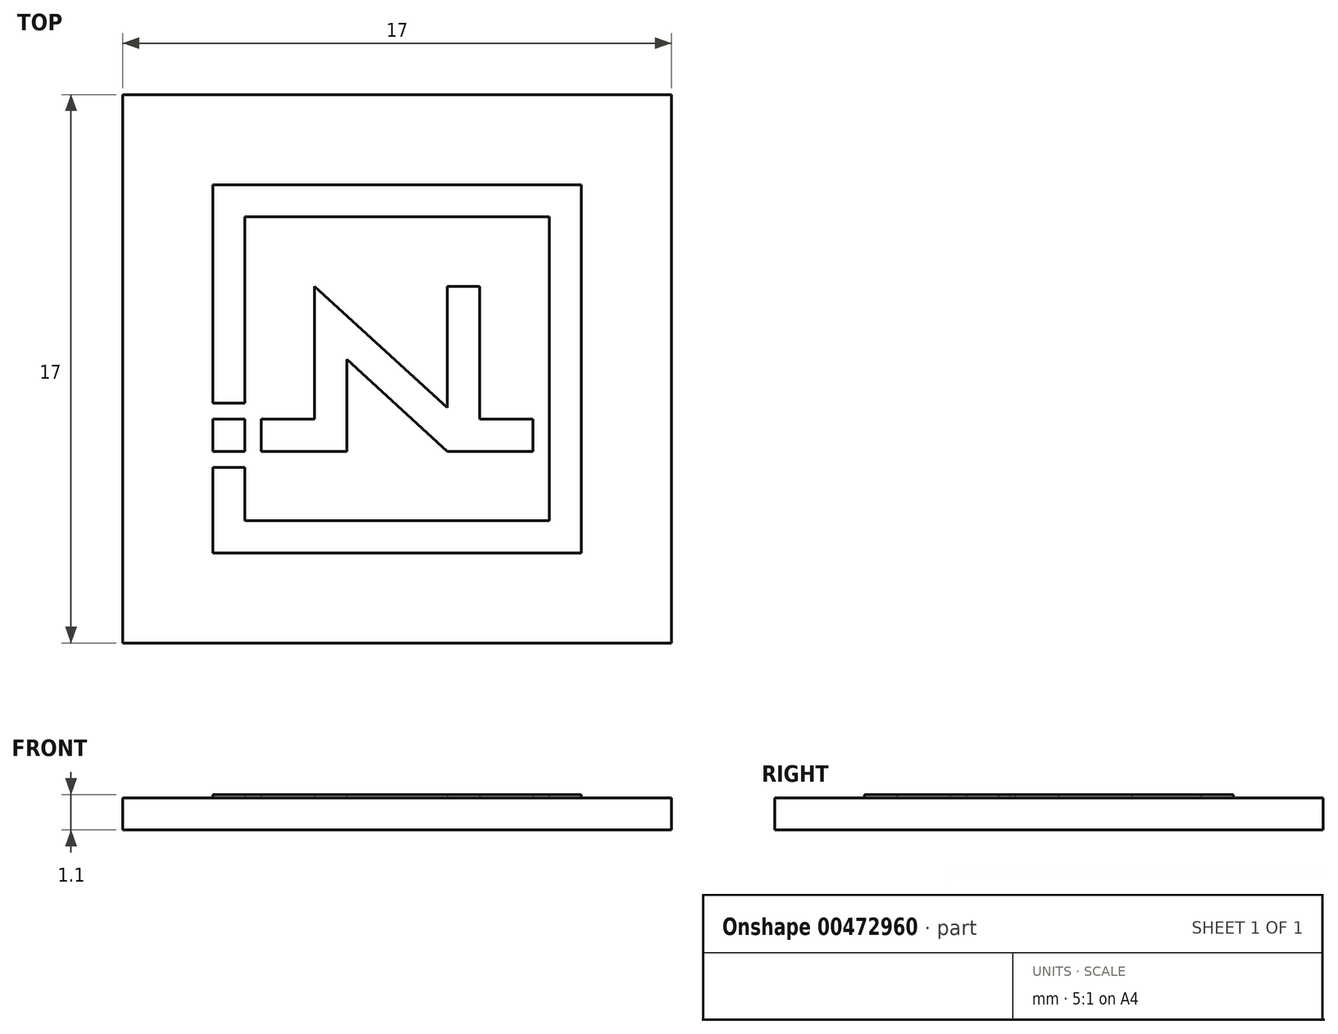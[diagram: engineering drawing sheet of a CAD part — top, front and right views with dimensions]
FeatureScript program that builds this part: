
annotation { "Feature Type Name" : "Feature", "Feature Type Description" : "" }
export const myFeature = defineFeature(function(context is Context, id is Id, definition is map)
    precondition{}
    {
        {
            var Q0;
            Q0=qCreatedBy(makeId("Top.planeOp"),FACE);
            var sketch = newSketch(context, id + "F0", { "sketchPlane" : qUnion([Q0])});
            skLineSegment(sketch, "E0.bottom", {"start": v(-5.71, 5.71) * mm, "end": v(5.71, 5.71) * mm});
            skLineSegment(sketch, "E0.top", {"start": v(-5.71, -5.71) * mm, "end": v(5.71, -5.71) * mm});
            skLineSegment(sketch, "E0.left", {"start": v(-5.71, 5.71) * mm, "end": v(-5.71, -5.71) * mm, "construction": true});
            skLineSegment(sketch, "E0.right", {"start": v(5.71, 5.71) * mm, "end": v(5.71, -5.71) * mm});
            skPoint(sketch, "E0.middle", {"position": v(0, 0) * mm});
            skLineSegment(sketch, "E1.0", {"start": v(4.71, 4.71) * mm, "end": v(4.71, -4.71) * mm});
            skLineSegment(sketch, "E1.1", {"start": v(-4.71, 4.71) * mm, "end": v(4.71, 4.71) * mm});
            skLineSegment(sketch, "E1.2", {"start": v(-4.71, 4.71) * mm, "end": v(-4.71, -4.71) * mm, "construction": true});
            skLineSegment(sketch, "E1.3", {"start": v(-4.71, -4.71) * mm, "end": v(4.71, -4.71) * mm});
            skLineSegment(sketch, "E2.bottom", {"start": v(8, 2.56) * mm, "end": v(-8, 2.56) * mm, "construction": true});
            skLineSegment(sketch, "E2.top", {"start": v(8, -2.56) * mm, "end": v(-8, -2.56) * mm, "construction": true});
            skLineSegment(sketch, "E2.left", {"start": v(8, 2.56) * mm, "end": v(8, -2.56) * mm, "construction": true});
            skLineSegment(sketch, "E2.right", {"start": v(-8, 2.56) * mm, "end": v(-8, -2.56) * mm, "construction": true});
            skLineSegment(sketch, "E3.bottom", {"start": v(-5.71, -2.56) * mm, "end": v(-4.71, -2.56) * mm});
            skLineSegment(sketch, "E3.top", {"start": v(-5.71, -1.56) * mm, "end": v(-4.71, -1.56) * mm});
            skLineSegment(sketch, "E3.left", {"start": v(-5.71, -2.56) * mm, "end": v(-5.71, -1.56) * mm});
            skLineSegment(sketch, "E3.right", {"start": v(-4.71, -2.56) * mm, "end": v(-4.71, -1.56) * mm});
            skLineSegment(sketch, "E4", {"start": v(-5.71, -5.71) * mm, "end": v(-5.71, -3.06) * mm});
            skLineSegment(sketch, "E5", {"start": v(-5.71, -3.06) * mm, "end": v(-4.71, -3.06) * mm});
            skLineSegment(sketch, "E6", {"start": v(-4.71, -3.06) * mm, "end": v(-4.71, -4.71) * mm});
            skLineSegment(sketch, "E7", {"start": v(-5.71, 5.71) * mm, "end": v(-5.71, -1.06) * mm});
            skLineSegment(sketch, "E8", {"start": v(-5.71, -1.06) * mm, "end": v(-4.71, -1.06) * mm});
            skLineSegment(sketch, "E9", {"start": v(-4.71, -1.06) * mm, "end": v(-4.71, 4.71) * mm});
            skLineSegment(sketch, "E10.bottom", {"start": v(-2.56, 2.56) * mm, "end": v(2.56, 2.56) * mm, "construction": true});
            skLineSegment(sketch, "E10.top", {"start": v(-2.56, -2.56) * mm, "end": v(2.56, -2.56) * mm, "construction": true});
            skLineSegment(sketch, "E10.left", {"start": v(-2.56, 2.56) * mm, "end": v(-2.56, -2.56) * mm, "construction": true});
            skLineSegment(sketch, "E10.right", {"start": v(2.56, 2.56) * mm, "end": v(2.56, -2.56) * mm, "construction": true});
            skLineSegment(sketch, "E11", {"start": v(-4.21, -2.56) * mm, "end": v(-4.21, -1.56) * mm});
            skLineSegment(sketch, "E12", {"start": v(-4.21, -1.56) * mm, "end": v(-2.56, -1.56) * mm});
            skLineSegment(sketch, "E13", {"start": v(-2.56, -1.56) * mm, "end": v(-2.56, 2.56) * mm});
            skLineSegment(sketch, "E14", {"start": v(-2.56, 2.56) * mm, "end": v(1.56, -1.2) * mm});
            skLineSegment(sketch, "E15", {"start": v(1.56, -1.2) * mm, "end": v(1.56, 2.56) * mm});
            skLineSegment(sketch, "E16", {"start": v(1.56, 2.56) * mm, "end": v(2.56, 2.56) * mm});
            skLineSegment(sketch, "E17", {"start": v(2.56, 2.56) * mm, "end": v(2.56, -1.56) * mm});
            skLineSegment(sketch, "E18", {"start": v(2.56, -1.56) * mm, "end": v(4.21, -1.56) * mm});
            skLineSegment(sketch, "E19", {"start": v(4.21, -1.56) * mm, "end": v(4.21, -2.56) * mm});
            skLineSegment(sketch, "E20", {"start": v(4.21, -2.56) * mm, "end": v(1.56, -2.56) * mm});
            skLineSegment(sketch, "E21", {"start": v(1.56, -2.56) * mm, "end": v(-1.56, 0.3) * mm});
            skLineSegment(sketch, "E22", {"start": v(-1.56, 0.3) * mm, "end": v(-1.56, -2.56) * mm});
            skLineSegment(sketch, "E23", {"start": v(-1.56, -2.56) * mm, "end": v(-4.21, -2.56) * mm});
            skSolve(sketch);
        }
        {
            var Q0;
            Q0 = qSketchRegion(id + "F0", true);
            extrude(context, id + "F1", {"entities" : qUnion([Q0]), "depth" : 0.1 * mm, "offsetDistance" : 25 * mm});
        }
        {
            var Q0;
            Q0=qCreatedBy(makeId("Top.planeOp"),FACE);
            var sketch = newSketch(context, id + "F2", { "sketchPlane" : qUnion([Q0])});
            skLineSegment(sketch, "E24.bottom", {"start": v(8.5, 8.5) * mm, "end": v(-8.5, 8.5) * mm});
            skLineSegment(sketch, "E24.top", {"start": v(8.5, -8.5) * mm, "end": v(-8.5, -8.5) * mm});
            skLineSegment(sketch, "E24.left", {"start": v(8.5, 8.5) * mm, "end": v(8.5, -8.5) * mm});
            skLineSegment(sketch, "E24.right", {"start": v(-8.5, 8.5) * mm, "end": v(-8.5, -8.5) * mm});
            skPoint(sketch, "E24.middle", {"position": v(0, 0) * mm});
            skSolve(sketch);
        }
        {
            var Q0;
            Q0 = qSketchRegion(id + "F2", true);
            var Q1;
            Q1 = qConstructionFilter(qBodyType(qCreatedBy(id + "F2" ,EDGE), BodyType.WIRE), ConstructionObject.NO);
            extrude(context, id + "F3", {"entities" : qUnion([Q0]), "surfaceEntities" : qUnion([Q1]), "oppositeDirection" : true, "depth" : 1 * mm, "offsetDistance" : 25 * mm});
        }
    });
